# Revit family: Cabinet_Wenger_UltraStor_62
name_source: partatom
category: Furniture
revit_build: Autodesk Revit 2015 (Build: 20140606_1530(x64)
units: mm (PartAtom-declared; Revit-internal decimal feet)

## types (1)
- UltraStor Cabinet #62 - Comp Wood Doors
    Assembly Code = E2010200
    Cabinet Height = 3' - 2 5/16"
    Cabinet Panel Thickness = 0' - 0 3/4"
    Cabinet Width = 3' - 0"
    Construction Details = http://www.arcat.com
    Cost = 0 $
    Description = Wenger UltraStor Cabinet #62 - Comp Wood Doors
    Door Height = 2' - 4 5/16"
    Door Width = 1' - 5 3/16"
    Green Building-LEED = http://www.arcat.com
    Installed Depth = 2' - 5 1/4"
    Keynote = 12 35 83
    Manufacturer = Wenger Corporation
    Manufacturer Fax = (507) 455-4258
    Manufacturer Website = https://www.wengercorp.com
    Model = #62
    Product Data = http://www.arcat.com
    Rear Panel Thickness = 0' - 0 3/4"
    Revision = R1_2018-04
    Sales Information = https://www.wengercorp.com
    Shelf Thickness = 0' - 1 1/8"
    Specification = http://www.arcat.com
    URL = https://www.wengercorp.com

## geometry (parser evidence)
native form markers: Blend x16, Sweep x8
no freeform markers — native parametric forms only
